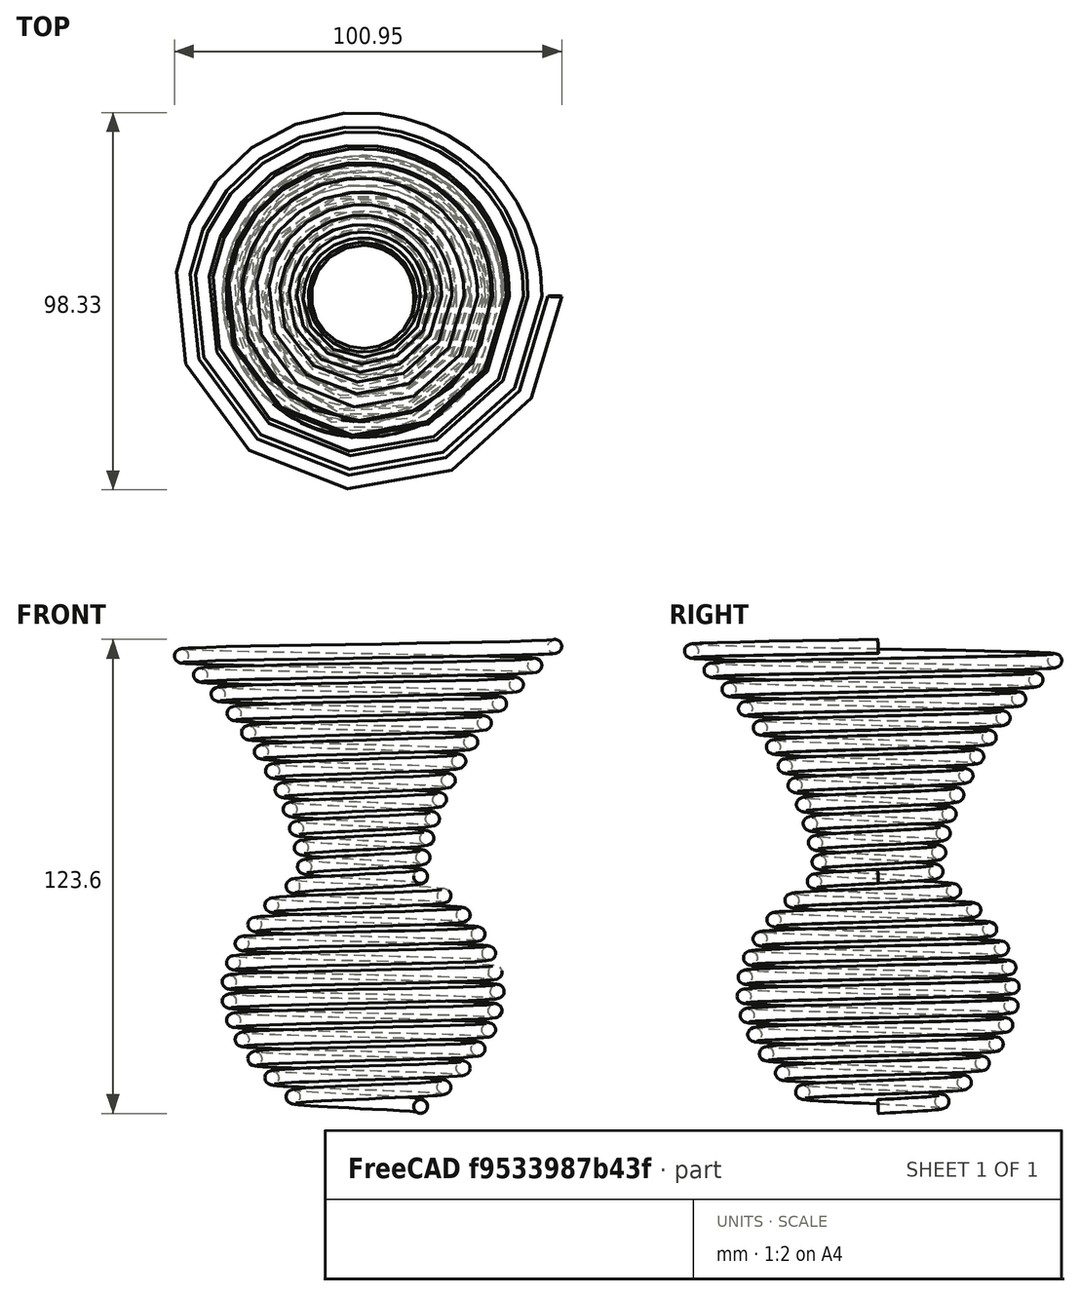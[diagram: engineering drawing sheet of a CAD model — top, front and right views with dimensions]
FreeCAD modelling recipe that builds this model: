
FCSTD DOCUMENT  (FreeCAD 0.19R17646 (Git))
Label: MOLA
License: All rights reserved
LicenseURL: http://en.wikipedia.org/wiki/All_rights_reserved
objects: Part::FeaturePython×5, Part::Sweep×2, Part::Helix×1, Part::Circle×1
note: 9 computed .brp shape members not serialized (recipe doc carries the construction recipe); baked Part::Feature solids carry a one-line shape summary decoded from their .brp

FEATURE [Part::Helix] Helix
  Angle = 0
  AttacherType = Attacher::AttachEngine3D
  Height = 60
  LocalCoord = 0
  Pitch = 5
  Radius = 15
  Style = 1
FEATURE [Part::Circle] Circle
  Angle0 = 0
  Angle1 = 360
  AttacherType = Attacher::AttachEngine3D
  Placement = pos=(15,0,0) rot=(1,0,0;4.76475rad)
  Radius = 1.8
FEATURE [Part::FeaturePython] Clone  label="Circle001"  # Draft clone (typed FeaturePython)
  AttacherType = Attacher::AttachEngine3D
  Fuse = false
  Objects = -> [Circle]
  Placement = pos=(35,6.7e-15,30) rot=(1,0,0;1.62316rad)
  Scale = (1,1,1)
FEATURE [Part::FeaturePython] Clone001  label="Circle002"  # Draft clone (typed FeaturePython)
  AttacherType = Attacher::AttachEngine3D
  Fuse = false
  Objects = -> [Clone]
  Placement = pos=(15,1.33e-14,60) rot=(1,0,0;1.62316rad)
  Scale = (1,1,1)
FEATURE [Part::Sweep] Sweep
  Frenet = true
  Sections = -> [Circle,Clone,Clone001]
  Solid = true
  Spine = -> Helix
  Transition = 0
FEATURE [Part::FeaturePython] Clone002  label="Circle003"  # Draft clone (typed FeaturePython)
  AttacherType = Attacher::AttachEngine3D
  Fuse = false
  Objects = -> [Circle]
  Placement = pos=(15,0,0) rot=(1,0,0;4.76475rad)
  Scale = (1,1,1)
FEATURE [Part::FeaturePython] Clone003  label="Circle004"  # Draft clone (typed FeaturePython)
  AttacherType = Attacher::AttachEngine3D
  Fuse = false
  Objects = -> [Clone]
  Placement = pos=(25,6.7e-15,30) rot=(1,0,0;1.62316rad)
  Scale = (1,1,1)
FEATURE [Part::FeaturePython] Clone004  label="Circle005"  # Draft clone (typed FeaturePython)
  AttacherType = Attacher::AttachEngine3D
  Fuse = false
  Objects = -> [Clone001]
  Placement = pos=(50,1.33e-14,60) rot=(1,0,0;1.62316rad)
  Scale = (1,1,1)
FEATURE [Part::Sweep] Sweep001
  Frenet = true
  Placement = pos=(0,0,60) rot=(0,0,1;0rad)
  Sections = -> [Clone004,Clone003,Clone002]
  Solid = true
  Spine = -> Helix
  Transition = 1
